annotation { "Feature Type Name" : "Feature", "Feature Type Description" : "" }
export const myFeature = defineFeature(function(context is Context, id is Id, definition is map)
    precondition{}
    {
        {
            var Q0;
            Q0=qCreatedBy(makeId("Front.planeOp"),FACE);
            var sketch = newSketch(context, id + "F0", { "sketchPlane" : qUnion([Q0])});
            skCircle(sketch, "E0", {"center": v(-63.7, 51.74) * mm, "radius": 5.84 * mm});
            skCircle(sketch, "E1", {"center": v(-47.42, 51.74) * mm, "radius": 6.12 * mm});
            skCircle(sketch, "E2", {"center": v(-31.66, 51.74) * mm, "radius": 7.1 * mm});
            skCircle(sketch, "E3", {"center": v(-14.3, 51.74) * mm, "radius": 7.3 * mm});
            skCircle(sketch, "E4", {"center": v(5, 51.74) * mm, "radius": 7.8 * mm});
            skSolve(sketch);
        }
        {
            var Q0;
            Q0=qCreatedBy(makeId("Front.planeOp"),FACE);
            var sketch = newSketch(context, id + "F1", { "sketchPlane" : qUnion([Q0])});
            skCircle(sketch, "E5", {"center": v(26.43, 52.61) * mm, "radius": 8.02 * mm});
            skCircle(sketch, "E6", {"center": v(44.5, 52.61) * mm, "radius": 8.22 * mm});
            skCircle(sketch, "E7", {"center": v(63.79, 52.61) * mm, "radius": 8.45 * mm});
            skText(sketch, "E8", { "text": "3", "fontName": "OpenSans-Bold.ttf"});
            skText(sketch, "E9", { "text": "3.5", "fontName": "OpenSans-Bold.ttf"});
            skText(sketch, "E10", { "text": "4", "fontName": "OpenSans-Bold.ttf"});
            skText(sketch, "E11", { "text": "4.5", "fontName": "OpenSans-Bold.ttf"});
            skText(sketch, "E12", { "text": "5", "fontName": "OpenSans-Bold.ttf"});
            skText(sketch, "E13", { "text": "5.5", "fontName": "OpenSans-Bold.ttf"});
            skText(sketch, "E14", { "text": "6", "fontName": "OpenSans-Bold.ttf"});
            skText(sketch, "E15", { "text": "6.5", "fontName": "OpenSans-Bold.ttf"});
            const initialGuessF1  = {"E8": [-0.06417, 0.038, 1, 0, 0.00555], "E9": [-0.04867, 0.03916, 1, 0, 0.00468], "E10": [-0.03288, 0.03712, 1, 0, 0.00526], "E11": [-0.01563, 0.0377, 1, 0, 0.00497], "E12": [0.00279, 0.0377, 1, 0, 0.00439], "E13": [0.02237, 0.0377, 1, 0, 0.00497], "E14": [0.0408, 0.03682, 1, 0, 0.00555], "E15": [0.06155, 0.03653, 1, 0, 0.00555]};
            skSetInitialGuess(sketch, initialGuessF1);
            skSolve(sketch);
        }
        {
            var Q0;
            Q0=qCreatedBy(makeId("Front.planeOp"),FACE);
            var sketch = newSketch(context, id + "F2", { "sketchPlane" : qUnion([Q0])});
            skCircle(sketch, "E16", {"center": v(-64.75, 23.76) * mm, "radius": 8.65 * mm});
            skCircle(sketch, "E17", {"center": v(-43.09, 23.76) * mm, "radius": 8.85 * mm});
            skSolve(sketch);
        }
        {
            var Q0;
            Q0=qCreatedBy(makeId("Front.planeOp"),FACE);
            var sketch = newSketch(context, id + "F3", { "sketchPlane" : qUnion([Q0])});
            skCircle(sketch, "E18", {"center": v(-20.41, 23.1) * mm, "radius": 9.1 * mm});
            skCircle(sketch, "E19", {"center": v(0, 23.1) * mm, "radius": 9.3 * mm});
            skSolve(sketch);
        }
        {
            var Q0;
            Q0=qCreatedBy(makeId("Front.planeOp"),FACE);
            var sketch = newSketch(context, id + "F4", { "sketchPlane" : qUnion([Q0])});
            skCircle(sketch, "E20", {"center": v(21.8, 23.72) * mm, "radius": 9.5 * mm});
            skCircle(sketch, "E21", {"center": v(47.02, 23.18) * mm, "radius": 9.7 * mm});
            skText(sketch, "E22", { "text": "7", "fontName": "OpenSans-Bold.ttf"});
            skText(sketch, "E23", { "text": "7.5", "fontName": "OpenSans-Bold.ttf"});
            skText(sketch, "E24", { "text": "8", "fontName": "OpenSans-Bold.ttf"});
            skText(sketch, "E25", { "text": "8.5", "fontName": "OpenSans-Bold.ttf"});
            skText(sketch, "E26", { "text": "9", "fontName": "OpenSans-Bold.ttf"});
            skText(sketch, "E27", { "text": "9.5", "fontName": "OpenSans-Bold.ttf"});
            const initialGuessF4  = {"E22": [-0.06642, 0.00604, 1, 0, 0.00714], "E23": [-0.04357, 0.00661, 1, 0, 0.00485], "E24": [-0.0213, 0.00518, 1, 0, 0.00743], "E25": [-0.00444, 0.00661, 1, 0, 0.00628], "E26": [0.01812, 0.00576, 1, 0, 0.00628], "E27": [0.0381, 0.00461, 1, 0, 0.00714]};
            skSetInitialGuess(sketch, initialGuessF4);
            skSolve(sketch);
        }
        {
            var Q0;
            Q0=qCreatedBy(makeId("Front.planeOp"),FACE);
            var sketch = newSketch(context, id + "F5", { "sketchPlane" : qUnion([Q0])});
            skCircle(sketch, "E28", {"center": v(70.83, 23.46) * mm, "radius": 9.9 * mm});
            skText(sketch, "E29", { "text": "10", "fontName": "OpenSans-Bold.ttf"});
            const initialGuessF5  = {"E29": [0.06442, 0.00452, 1, 0, 0.00583]};
            skSetInitialGuess(sketch, initialGuessF5);
            skSolve(sketch);
        }
        {
            var Q0;
            Q0=qCreatedBy(makeId("Front.planeOp"),FACE);
            var sketch = newSketch(context, id + "F6", { "sketchPlane" : qUnion([Q0])});
            skCircle(sketch, "E30", {"center": v(-64.7, -12.39) * mm, "radius": 10.1 * mm});
            skCircle(sketch, "E31", {"center": v(-36.43, -12.39) * mm, "radius": 10.3 * mm});
            skCircle(sketch, "E32", {"center": v(-9.04, -12.39) * mm, "radius": 10.5 * mm});
            skCircle(sketch, "E33", {"center": v(22.15, -12.39) * mm, "radius": 10.7 * mm});
            skCircle(sketch, "E34", {"center": v(48.97, -12.39) * mm, "radius": 10.9 * mm});
            skCircle(sketch, "E35", {"center": v(75.5, -12.39) * mm, "radius": 11.1 * mm});
            skCircle(sketch, "E36", {"center": v(0, -49.7) * mm, "radius": 11.3 * mm});
            skText(sketch, "E37", { "text": "10.5", "fontName": "OpenSans-Bold.ttf"});
            skText(sketch, "E38", { "text": "11", "fontName": "OpenSans-Bold.ttf"});
            skText(sketch, "E39", { "text": "11.5", "fontName": "OpenSans-Bold.ttf"});
            skText(sketch, "E40", { "text": "12", "fontName": "OpenSans-Bold.ttf"});
            skText(sketch, "E41", { "text": "12.5", "fontName": "OpenSans-Bold.ttf"});
            skText(sketch, "E42", { "text": "13", "fontName": "OpenSans-Bold.ttf"});
            skText(sketch, "E43", { "text": "13.5", "fontName": "OpenSans-Bold.ttf"});
            const initialGuessF6  = {"E37": [-0.07083, -0.03075, 1, 0, 0.00554], "E38": [-0.03906, -0.03163, 1, 0, 0.0067], "E39": [-0.0134, -0.03163, 1, 0, 0.00583], "E40": [0.01895, -0.03104, 1, 0, 0.00554], "E41": [0.0446, -0.03192, 1, 0, 0.00583], "E42": [0.072, -0.03337, 1, 0, 0.007], "E43": [-0.01166, -0.06952, 1, 0, 0.00758]};
            skSetInitialGuess(sketch, initialGuessF6);
            skSolve(sketch);
        }
        {
            var Q0;
            Q0=qCreatedBy(makeId("Front.planeOp"),FACE);
            var sketch = newSketch(context, id + "F7", { "sketchPlane" : qUnion([Q0])});
            skText(sketch, "E44", { "text": "Ring Sizes", "fontName": "OpenSans-Bold.ttf"});
            const initialGuessF7  = {"E44": [-0.03323, 0.06194, 1, 0, 0.01078]};
            skSetInitialGuess(sketch, initialGuessF7);
            skSolve(sketch);
        }
        {
            var Q0;
            Q0 = qSketchRegion(id + "F0", true);
            extrude(context, id + "F8", {"entities" : qUnion([Q0]), "depth" : 0.25 * mm});
        }
        {
            var Q0;
            Q0 = qSketchRegion(id + "F1", true);
            extrude(context, id + "F9", {"entities" : qUnion([Q0]), "depth" : 0.25 * mm});
        }
        {
            var Q0;
            Q0 = qSketchRegion(id + "F2", true);
            var Q1;
            Q1 = qSketchRegion(id + "F3", true);
            var Q2;
            Q2 = qSketchRegion(id + "F4", true);
            var Q3;
            Q3 = qSketchRegion(id + "F5", true);
            var Q4;
            Q4 = qSketchRegion(id + "F6", true);
            extrude(context, id + "F10", {"entities" : qUnion([Q0, Q1, Q2, Q3, Q4]), "depth" : 0.25 * mm});
        }
        {
            var Q0;
            Q0 = qSketchRegion(id + "F7", true);
            extrude(context, id + "F11", {"entities" : qUnion([Q0]), "depth" : 0.25 * mm});
        }
    });